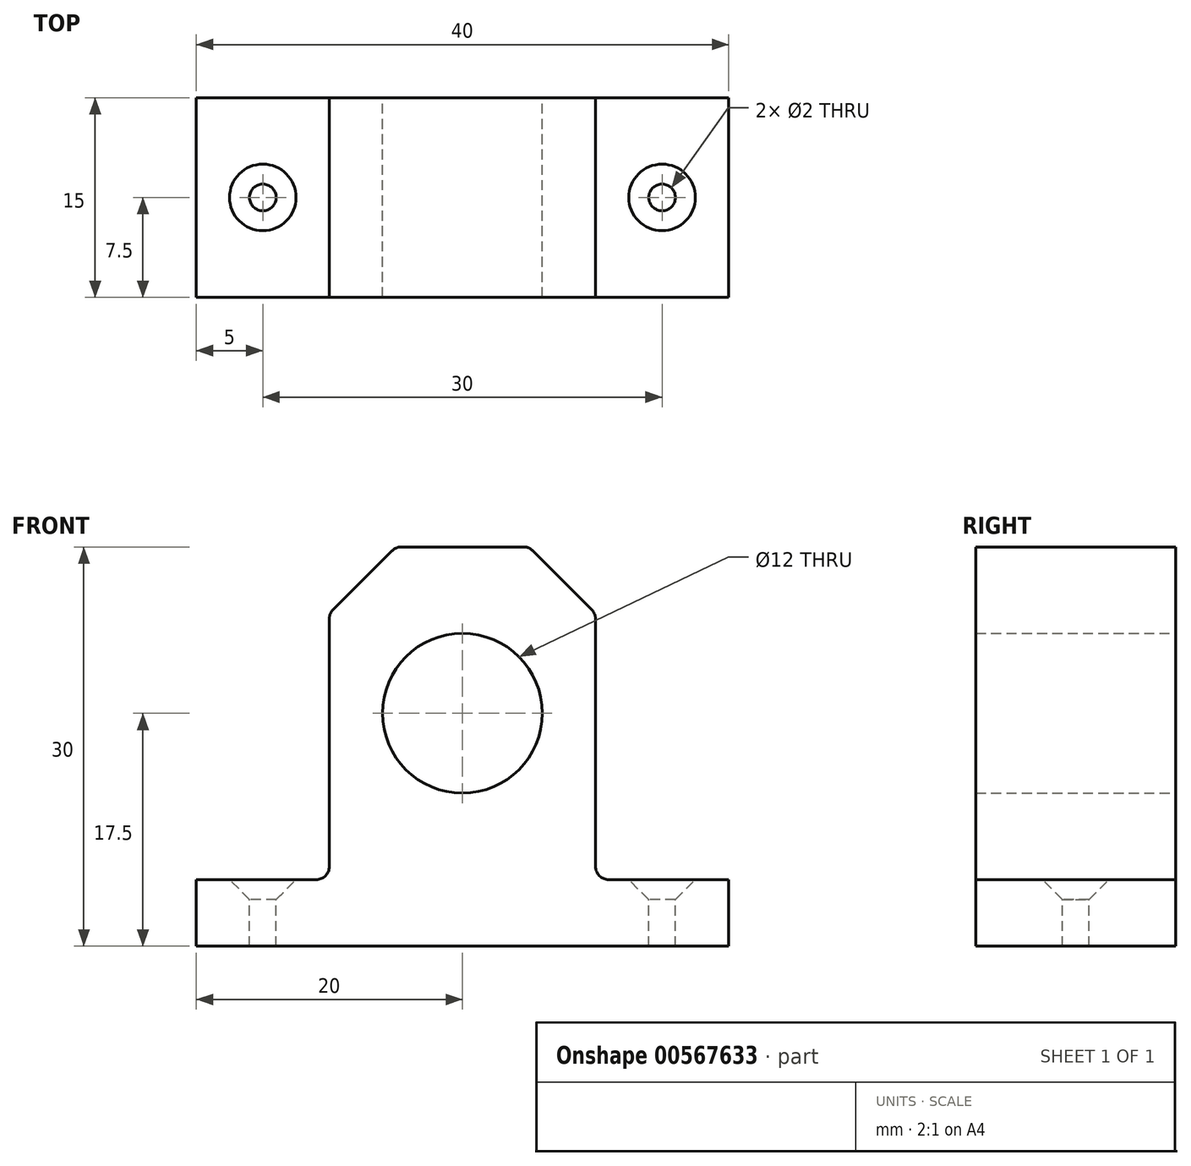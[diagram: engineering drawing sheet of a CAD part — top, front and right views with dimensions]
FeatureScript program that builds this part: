
annotation { "Feature Type Name" : "Feature", "Feature Type Description" : "" }
export const myFeature = defineFeature(function(context is Context, id is Id, definition is map)
    precondition{}
    {
        {
            var Q0;
            Q0=qCreatedBy(makeId("Front.planeOp"),FACE);
            var sketch = newSketch(context, id + "F0", { "sketchPlane" : qUnion([Q0])});
            skCircle(sketch, "E0", {"center": v(0, 0) * mm, "radius": 6 * mm});
            skLineSegment(sketch, "E1.bottom", {"start": v(10, -12.5) * mm, "end": v(-10, -12.5) * mm});
            skLineSegment(sketch, "E1.top", {"start": v(10, 12.5) * mm, "end": v(-10, 12.5) * mm});
            skLineSegment(sketch, "E1.left", {"start": v(10, -12.5) * mm, "end": v(10, 12.5) * mm});
            skLineSegment(sketch, "E1.right", {"start": v(-10, -12.5) * mm, "end": v(-10, 12.5) * mm});
            skLineSegment(sketch, "E2.bottom", {"start": v(20, -12.5) * mm, "end": v(-20, -12.5) * mm});
            skLineSegment(sketch, "E2.top", {"start": v(20, -17.5) * mm, "end": v(-20, -17.5) * mm});
            skLineSegment(sketch, "E2.left", {"start": v(20, -12.5) * mm, "end": v(20, -17.5) * mm});
            skLineSegment(sketch, "E2.right", {"start": v(-20, -12.5) * mm, "end": v(-20, -17.5) * mm});
            skPoint(sketch, "E2.middle", {"position": v(0, -15) * mm});
            skSolve(sketch);
        }
        {
            var Q0;
            Q0=makeQuery(id+"F0.imprint","IMPRINT",FACE,{"disambiguationData":[TD([[makeQuery(id+"F0.imprint","IMPRINT",EDGE,{"derivedFrom":sQuery(id+"F0.wireOp",EDGE,"E0")}),-1.0]])]});
            var Q1;
            Q1=makeQuery(id+"F0.imprint","IMPRINT",FACE,{"disambiguationData":[TD([[makeQuery(id+"F0.imprint","IMPRINT",EDGE,{"derivedFrom":sQuery(id+"F0.wireOp",EDGE,"E2.top")}),-1.0]])]});
            extrude(context, id + "F1", {"entities" : qUnion([Q0, Q1]), "depth" : 15 * mm, "offsetDistance" : 25 * mm});
        }
        {
            var Q0;
            Q0=makeQuery(id+"F1.opExtrude","SWEPT_EDGE",EDGE,{"disambiguationData":[OSD([sQuery(id+"F0.wireOp",EDGE,"E1.top"),sQuery(id+"F0.wireOp",EDGE,"E1.left")])]});
            var Q1;
            Q1=makeQuery(id+"F1.opExtrude","SWEPT_EDGE",EDGE,{"disambiguationData":[OSD([sQuery(id+"F0.wireOp",EDGE,"E1.top"),sQuery(id+"F0.wireOp",EDGE,"E1.right")])]});
            chamfer(context, id + "F2", {"entities" : qUnion([Q0, Q1]), "width" : 5 * mm, "tangentPropagation" : true});
        }
        {
            var Q0;
            {var subQ0=sQuery(id+"F0.wireOp",EDGE,"E2.bottom");Q0=makeQuery(id+"F1.opExtrude","SWEPT_FACE",FACE,{"disambiguationData":[OSD([subQ0]),TDD([makeQuery(id+"F0.imprint","IMPRINT",EDGE,{"disambiguationData":[TD([[makeQuery(id+"F0.imprint","INTERSECT",VERTEX,{"derivedFrom":[sQuery(id+"F0.wireOp",EDGE,"E1.right"),subQ0]}),-1.0]])],"derivedFrom":subQ0})])]});}
            var sketch = newSketch(context, id + "F3", { "sketchPlane" : qUnion([Q0])});
            skPoint(sketch, "E3", {"position": v(-15, -7.5) * mm});
            skPoint(sketch, "E3.positionSnap0", {"position": v(-20, -7.5) * mm});
            skPoint(sketch, "E3.positionSnap1", {"position": v(-15, 0) * mm});
            skPoint(sketch, "E4", {"position": v(15, -7.5) * mm});
            skSolve(sketch);
        }
        {
            var Q0;
            Q0=sQuery(id+"F3.wireOp",VERTEX,"E4");
            var Q1;
            Q1=sQuery(id+"F3.wireOp",VERTEX,"E3");
            var Q2;
            Q2=makeQuery(id+"F1.opExtrude","SWEPT_BODY",BODY,{"disambiguationData":[OSD([sQuery(id+"F0.wireOp",EDGE,"E0"),sQuery(id+"F0.wireOp",EDGE,"E1.top"),sQuery(id+"F0.wireOp",EDGE,"E1.left"),sQuery(id+"F0.wireOp",EDGE,"E1.right"),sQuery(id+"F0.wireOp",EDGE,"E2.bottom"),sQuery(id+"F0.wireOp",EDGE,"E2.top"),sQuery(id+"F0.wireOp",EDGE,"E2.left"),sQuery(id+"F0.wireOp",EDGE,"E2.right")])]});
            hole(context, id + "F4", {"style" : HoleStyle.C_SINK, "endStyle" : HoleEndStyle.THROUGH, "holeDiameter" : 2 * mm, "cSinkDiameter" : 5 * mm, "cSinkAngle" : 90 * degree, "majorDiameter" : 5 * mm, "isTappedThrough" : true, "tappedDepth" : 12 * mm, "tapClearance" : 3, "locations" : qUnion([Q0, Q1]), "scope" : qUnion([Q2])});
        }
        {
            var Q0;
            Q0=makeQuery(id+"F1.opExtrude","SWEPT_EDGE",EDGE,{"disambiguationData":[OSD([sQuery(id+"F0.wireOp",EDGE,"E1.right"),sQuery(id+"F0.wireOp",EDGE,"E2.bottom")])]});
            var Q1;
            {var subQ0=sQuery(id+"F0.wireOp",EDGE,"E1.right");Q1=makeQuery(id+"F2.opChamfer","BLEND_EDGE",EDGE,{"blendedFrom":[makeQuery(id+"F1.opExtrude","SWEPT_EDGE",EDGE,{"disambiguationData":[OSD([sQuery(id+"F0.wireOp",EDGE,"E1.top"),subQ0])]}),makeQuery(id+"F1.opExtrude","SWEPT_FACE",FACE,{"disambiguationData":[OSD([subQ0])]})],"blendedInto":[makeQuery(id+"F1.opExtrude","SWEPT_FACE",FACE,{"disambiguationData":[OSD([subQ0])]})]});}
            var Q2;
            {var subQ0=sQuery(id+"F0.wireOp",EDGE,"E1.top");Q2=makeQuery(id+"F2.opChamfer","BLEND_EDGE",EDGE,{"blendedFrom":[makeQuery(id+"F1.opExtrude","SWEPT_EDGE",EDGE,{"disambiguationData":[OSD([subQ0,sQuery(id+"F0.wireOp",EDGE,"E1.right")])]}),makeQuery(id+"F1.opExtrude","SWEPT_FACE",FACE,{"disambiguationData":[OSD([subQ0])]})],"blendedInto":[makeQuery(id+"F1.opExtrude","SWEPT_FACE",FACE,{"disambiguationData":[OSD([subQ0])]})]});}
            var Q3;
            {var subQ0=sQuery(id+"F0.wireOp",EDGE,"E1.top");Q3=makeQuery(id+"F2.opChamfer","BLEND_EDGE",EDGE,{"blendedFrom":[makeQuery(id+"F1.opExtrude","SWEPT_EDGE",EDGE,{"disambiguationData":[OSD([subQ0,sQuery(id+"F0.wireOp",EDGE,"E1.left")])]}),makeQuery(id+"F1.opExtrude","SWEPT_FACE",FACE,{"disambiguationData":[OSD([subQ0])]})],"blendedInto":[makeQuery(id+"F1.opExtrude","SWEPT_FACE",FACE,{"disambiguationData":[OSD([subQ0])]})]});}
            var Q4;
            {var subQ0=sQuery(id+"F0.wireOp",EDGE,"E1.left");Q4=makeQuery(id+"F2.opChamfer","BLEND_EDGE",EDGE,{"blendedFrom":[makeQuery(id+"F1.opExtrude","SWEPT_EDGE",EDGE,{"disambiguationData":[OSD([sQuery(id+"F0.wireOp",EDGE,"E1.top"),subQ0])]}),makeQuery(id+"F1.opExtrude","SWEPT_FACE",FACE,{"disambiguationData":[OSD([subQ0])]})],"blendedInto":[makeQuery(id+"F1.opExtrude","SWEPT_FACE",FACE,{"disambiguationData":[OSD([subQ0])]})]});}
            var Q5;
            Q5=makeQuery(id+"F1.opExtrude","SWEPT_EDGE",EDGE,{"disambiguationData":[OSD([sQuery(id+"F0.wireOp",EDGE,"E1.left"),sQuery(id+"F0.wireOp",EDGE,"E2.bottom")])]});
            fillet(context, id + "F5", {"entities" : qUnion([Q0, Q1, Q2, Q3, Q4, Q5]), "radius" : 1 * mm, "tangentPropagation" : true, "allowEdgeOverflow" : false});
        }
    });
